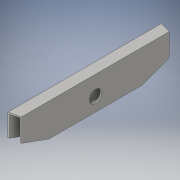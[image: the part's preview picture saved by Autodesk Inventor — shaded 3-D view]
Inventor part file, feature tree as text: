
AUTODESK INVENTOR PART (.ipt)
format: ipt  version: 2016 (Build 200138000, 138)  size: 107,520 bytes
history: native  units: in
note: dims shown in document units (in); Inventor stores cm internally (conversion verified against a paired STEP export)
features: sketch x1, projected_geometry x1, imported_body x1
ambient origin geometry x8: Origin, YZ Plane, XZ Plane, XY Plane, X Axis, Y Axis, Z Axis, Center Point
bodies: Solid1 (feature_tree)
feature tree (3):
  sketch  "Sketch1"  dims[d0=0.6875in]
  projected_geometry  "Projected Loop1"
  imported_body  "Base1"
